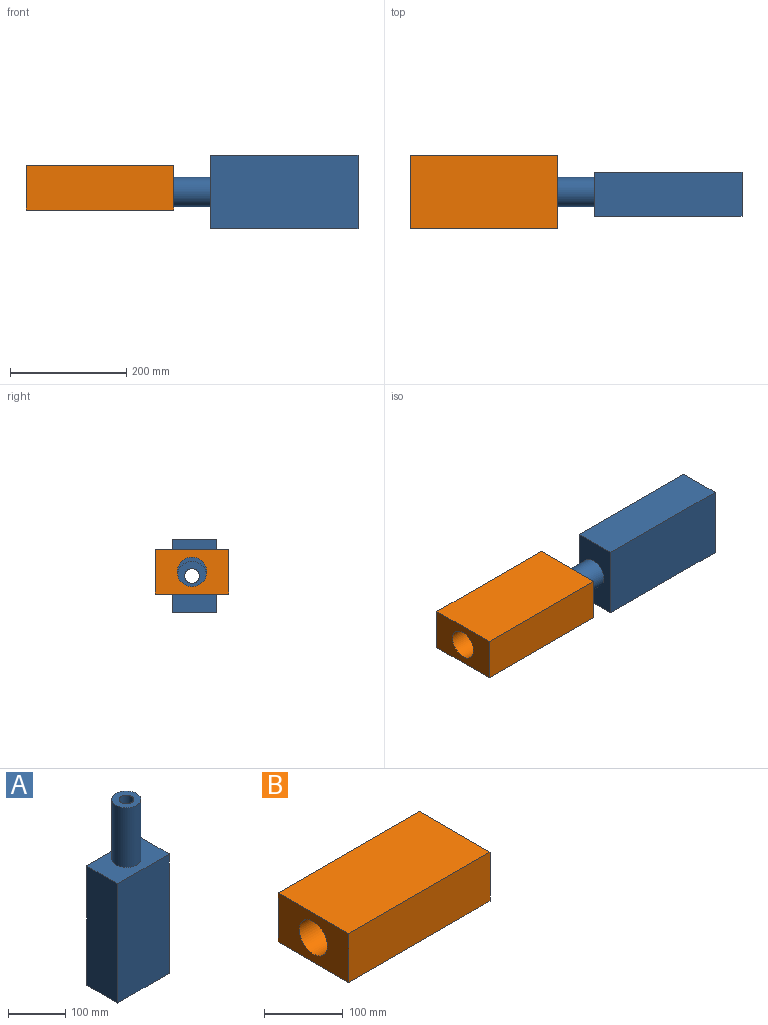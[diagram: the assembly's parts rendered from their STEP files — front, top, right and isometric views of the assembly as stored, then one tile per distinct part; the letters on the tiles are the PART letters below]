
ASSEMBLY  parts=2 mates=1
PART A: 9 faces, bbox 127x76.2x381 mm
  f0: plane 254x127mm, normal (0,1,0), area 32258mm2, adj f1,f3,f4,f5
  f1: plane 254x76.2mm, normal (-1,0,0), area 19354.8mm2, adj f0,f2,f4,f5
  f2: plane 254x127mm, normal (0,-1,0), area 32258mm2, adj f1,f3,f4,f5
  f3: plane 254x76.2mm, normal (1,0,0), area 19354.8mm2, adj f0,f2,f4,f5
  f4: plane 127x76.2mm, normal (0,0,1), area 7650.6mm2, adj f0,f1,f2,f3,f6
  f5: plane 127x76.2mm, normal (0,0,-1), area 9170.7mm2, adj f0,f1,f2,f3,f8
  f6: cylinder r=25.4mm len=127mm, axis (0,0,-1), area 20268.3mm2, adj f4,f7
  f7: plane 50.8x50.8mm, normal (0,0,1), area 1520.1mm2, adj f6,f8
  f8: cylinder r=12.7mm len=381mm, axis (0,0,-1), area 30402.4mm2, adj f5,f7
PART B: 7 faces, bbox 254x127x76.2 mm
  f0: plane 254x76.2mm, normal (0,1,0), area 19354.8mm2, adj f1,f3,f4,f5
  f1: plane 127x76.2mm, normal (-1,0,0), area 7650.6mm2, adj f0,f2,f4,f5,f6
  f2: plane 254x76.2mm, normal (0,-1,0), area 19354.8mm2, adj f1,f3,f4,f5
  f3: plane 127x76.2mm, normal (1,0,0), area 7650.6mm2, adj f0,f2,f4,f5,f6
  f4: plane 254x127mm, normal (0,0,1), area 32258mm2, adj f0,f1,f2,f3
  f5: plane 254x127mm, normal (0,0,-1), area 32258mm2, adj f0,f1,f2,f3
  f6: cylinder r=25.4mm len=254mm, axis (1,0,0), area 40536.6mm2, adj f1,f3
PLACE A rot(axis=(0,-1,0),90deg) t=(112.27,-77.69,264.59)mm
PLACE B t=(-334.26,-79.18,233.59)mm
MATE pin_slot A.f6 <-> B.f6  axis (1,0,0) through (-205.23,-77.69,264.59)mm
